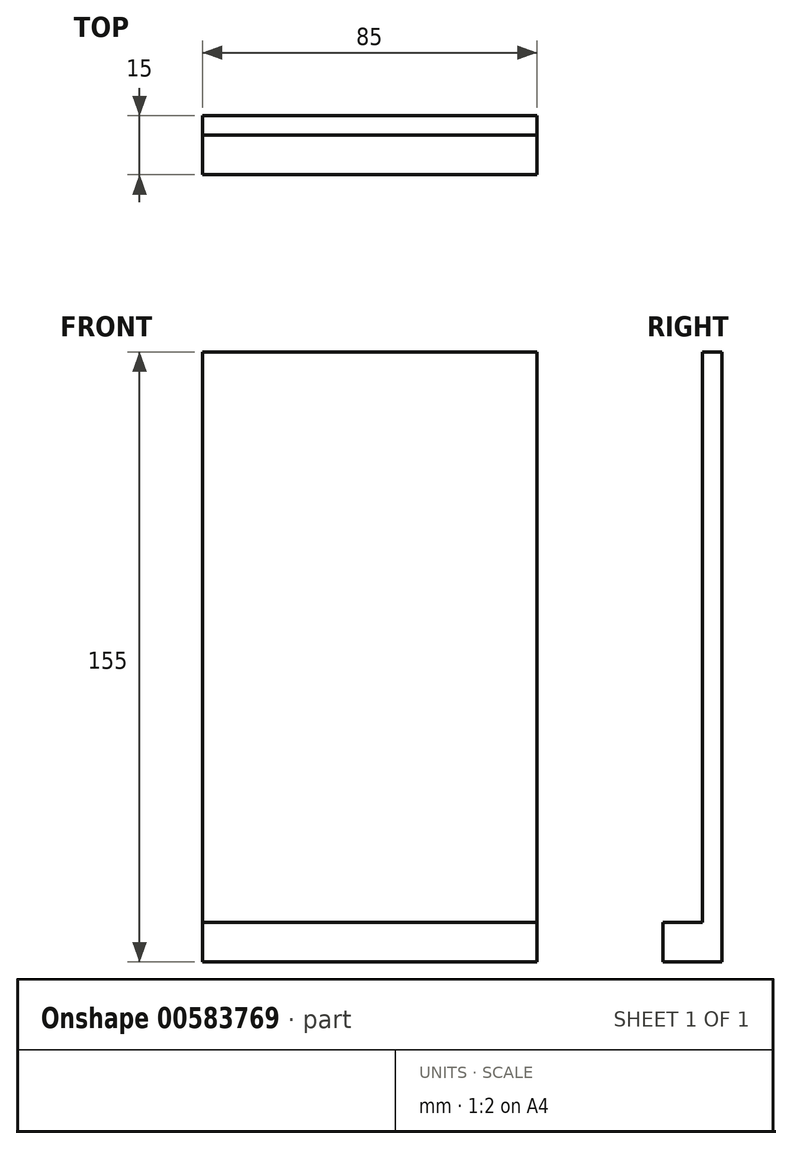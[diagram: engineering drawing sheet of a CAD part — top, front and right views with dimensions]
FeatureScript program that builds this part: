
annotation { "Feature Type Name" : "Feature", "Feature Type Description" : "" }
export const myFeature = defineFeature(function(context is Context, id is Id, definition is map)
    precondition{}
    {
        {
            var Q0;
            Q0=qCreatedBy(makeId("Front.planeOp"),FACE);
            var sketch = newSketch(context, id + "F0", { "sketchPlane" : qUnion([Q0])});
            skLineSegment(sketch, "E0.bottom", {"start": v(-39.97, -72.45) * mm, "end": v(45.03, -72.45) * mm});
            skPoint(sketch, "E0.middle", {"position": v(0, 0) * mm});
            skLineSegment(sketch, "E1", {"start": v(-39.97, -62.45) * mm, "end": v(45.03, -62.45) * mm});
            skLineSegment(sketch, "E2", {"start": v(45.03, -72.45) * mm, "end": v(45.03, -62.45) * mm});
            skLineSegment(sketch, "E3", {"start": v(-39.97, -72.45) * mm, "end": v(-39.97, -62.45) * mm});
            skLineSegment(sketch, "E4", {"start": v(-39.97, 82.55) * mm, "end": v(45.03, 82.55) * mm});
            skLineSegment(sketch, "E5", {"start": v(-39.97, 82.55) * mm, "end": v(-39.97, -62.45) * mm});
            skLineSegment(sketch, "E6", {"start": v(45.03, 82.55) * mm, "end": v(45.03, -62.45) * mm});
            skSolve(sketch);
        }
        {
            var Q0;
            Q0=makeQuery(id+"F0.imprint","IMPRINT",FACE,{"disambiguationData":[TD([[makeQuery(id+"F0.imprint","IMPRINT",EDGE,{"derivedFrom":sQuery(id+"F0.wireOp",EDGE,"E1")}),1.0]])]});
            extrude(context, id + "F1", {"entities" : qUnion([Q0]), "depth" : 5 * mm, "offsetDistance" : 25 * mm});
        }
        {
            var Q0;
            Q0=makeQuery(id+"F0.imprint","IMPRINT",FACE,{"disambiguationData":[TD([[makeQuery(id+"F0.imprint","IMPRINT",EDGE,{"derivedFrom":sQuery(id+"F0.wireOp",EDGE,"E0.bottom")}),1.0]])]});
            extrude(context, id + "F2", {"entities" : qUnion([Q0]), "operationType" : NewBodyOperationType.ADD, "depth" : 15 * mm, "offsetDistance" : 25 * mm});
        }
    });
